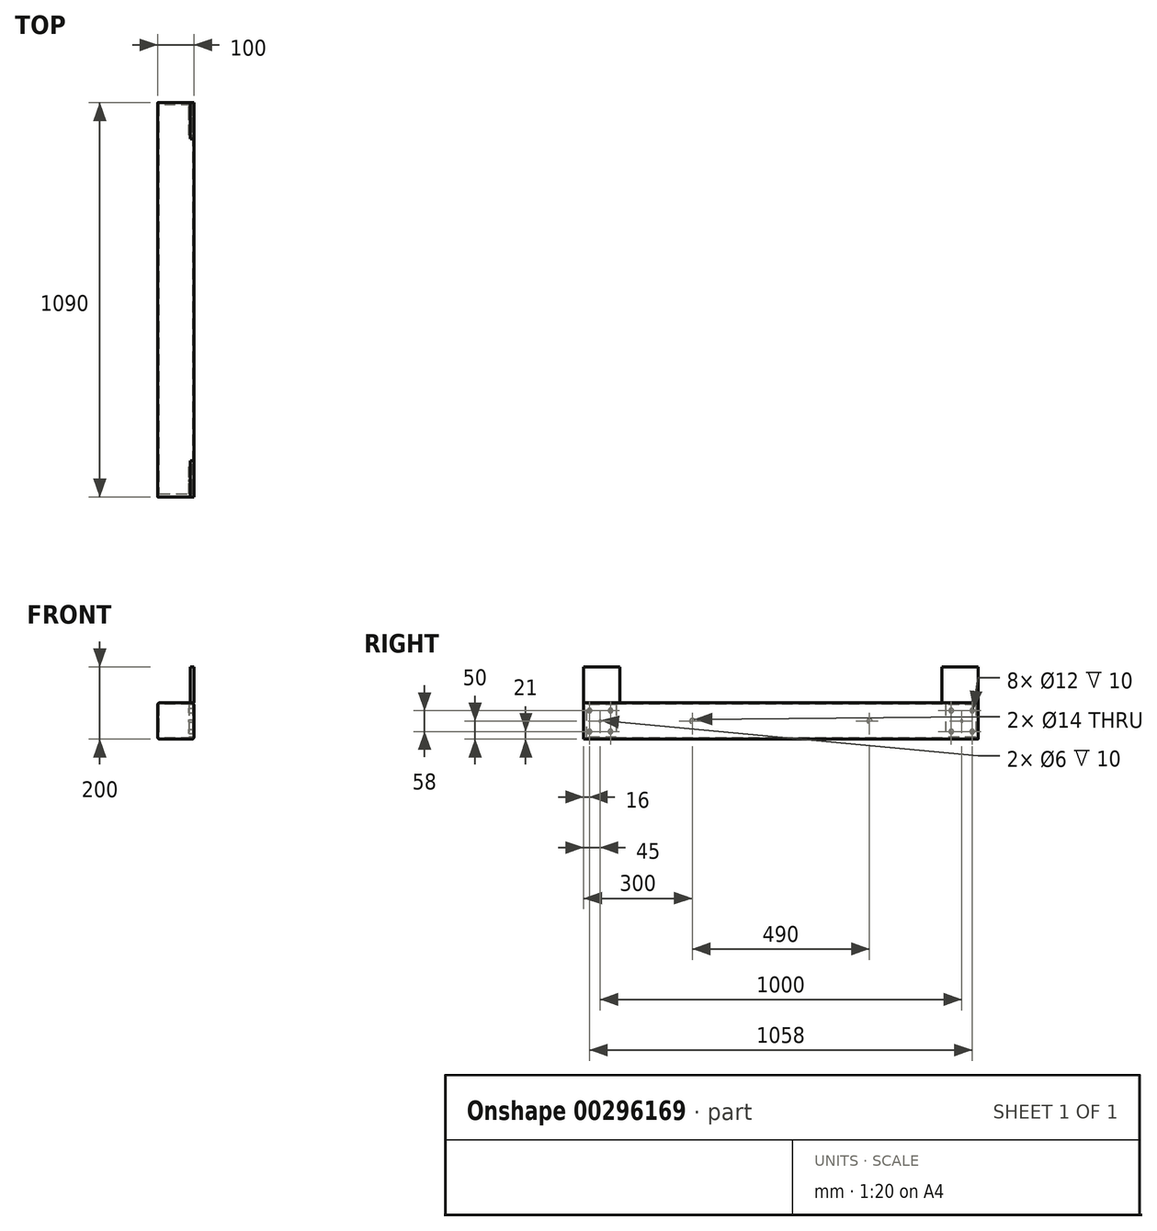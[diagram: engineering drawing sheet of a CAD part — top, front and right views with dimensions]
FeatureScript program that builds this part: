
annotation { "Feature Type Name" : "Feature", "Feature Type Description" : "" }
export const myFeature = defineFeature(function(context is Context, id is Id, definition is map)
    precondition{}
    {
        {
            var Q0;
            Q0=qCreatedBy(makeId("Front.planeOp"),FACE);
            var sketch = newSketch(context, id + "F0", { "sketchPlane" : qUnion([Q0])});
            skLineSegment(sketch, "E0.bottom", {"start": v(45, 50) * mm, "end": v(-45, 50) * mm});
            skLineSegment(sketch, "E0.top", {"start": v(45, -50) * mm, "end": v(-45, -50) * mm});
            skLineSegment(sketch, "E0.left", {"start": v(50, 45) * mm, "end": v(50, -45) * mm});
            skLineSegment(sketch, "E0.right", {"start": v(-50, 45) * mm, "end": v(-50, -45) * mm});
            skPoint(sketch, "E0.middle", {"position": v(0, 0) * mm});
            skPoint(sketch, "E1.visualSharp", {"position": v(-50, 50) * mm});
            skArc(sketch, "E1.filletArc", {"start": v(-45, 50) * mm, "mid": v(-48.54, 48.54) * mm, "end": v(-50, 45) * mm});
            skPoint(sketch, "E2.visualSharp", {"position": v(50, 50) * mm});
            skArc(sketch, "E2.filletArc", {"start": v(50, 45) * mm, "mid": v(48.54, 48.54) * mm, "end": v(45, 50) * mm});
            skPoint(sketch, "E3.visualSharp", {"position": v(50, -50) * mm});
            skArc(sketch, "E3.filletArc", {"start": v(45, -50) * mm, "mid": v(48.54, -48.54) * mm, "end": v(50, -45) * mm});
            skPoint(sketch, "E4.visualSharp", {"position": v(-50, -50) * mm});
            skArc(sketch, "E4.filletArc", {"start": v(-50, -45) * mm, "mid": v(-48.54, -48.54) * mm, "end": v(-45, -50) * mm});
            skArc(sketch, "E5.0", {"start": v(-45, 47) * mm, "mid": v(-46.41, 46.41) * mm, "end": v(-47, 45) * mm});
            skLineSegment(sketch, "E5.1", {"start": v(45, 47) * mm, "end": v(-45, 47) * mm});
            skLineSegment(sketch, "E5.2", {"start": v(-47, 45) * mm, "end": v(-47, -45) * mm});
            skArc(sketch, "E5.3", {"start": v(47, 45) * mm, "mid": v(46.41, 46.41) * mm, "end": v(45, 47) * mm});
            skArc(sketch, "E5.4", {"start": v(-47, -45) * mm, "mid": v(-46.41, -46.41) * mm, "end": v(-45, -47) * mm});
            skLineSegment(sketch, "E5.5", {"start": v(45, -47) * mm, "end": v(-45, -47) * mm});
            skArc(sketch, "E5.6", {"start": v(45, -47) * mm, "mid": v(46.41, -46.41) * mm, "end": v(47, -45) * mm});
            skLineSegment(sketch, "E5.7", {"start": v(47, 45) * mm, "end": v(47, -45) * mm});
            skSolve(sketch);
        }
        {
            var Q0;
            Q0=makeQuery(id+"F0.imprint","IMPRINT",FACE,{"disambiguationData":[TD([[makeQuery(id+"F0.imprint","IMPRINT",EDGE,{"derivedFrom":sQuery(id+"F0.wireOp",EDGE,"E0.bottom")}),1.0]])]});
            extrude(context, id + "F1", {"entities" : qUnion([Q0]), "oppositeDirection" : true, "depth" : (800 + 100 + 100 * 2 - 2 * 5 - 2 * 6) * mm});
        }
        {
            var Q0;
            Q0=makeQuery(id+"F1.opExtrude","CAP_FACE",FACE,{"disambiguationData":[OSD([sQuery(id+"F0.wireOp",EDGE,"E0.bottom"),sQuery(id+"F0.wireOp",EDGE,"E0.top"),sQuery(id+"F0.wireOp",EDGE,"E0.left"),sQuery(id+"F0.wireOp",EDGE,"E0.right"),sQuery(id+"F0.wireOp",EDGE,"E1.filletArc"),sQuery(id+"F0.wireOp",EDGE,"E2.filletArc"),sQuery(id+"F0.wireOp",EDGE,"E3.filletArc"),sQuery(id+"F0.wireOp",EDGE,"E4.filletArc"),sQuery(id+"F0.wireOp",EDGE,"E5.0"),sQuery(id+"F0.wireOp",EDGE,"E5.1"),sQuery(id+"F0.wireOp",EDGE,"E5.2"),sQuery(id+"F0.wireOp",EDGE,"E5.3"),sQuery(id+"F0.wireOp",EDGE,"E5.4"),sQuery(id+"F0.wireOp",EDGE,"E5.5"),sQuery(id+"F0.wireOp",EDGE,"E5.6"),sQuery(id+"F0.wireOp",EDGE,"E5.7")])],"isStart":true});
            cPlane(context, id + "F2", {"entities" : qUnion([Q0]), "cplaneType" : CPlaneType.OFFSET, "offset" : 6 * mm, "width" : 150 * mm, "height" : 150 * mm});
        }
        {
            var Q0;
            Q0=qCreatedBy(id+"F2.planeOp",FACE);
            var sketch = newSketch(context, id + "F3", { "sketchPlane" : qUnion([Q0])});
            skLineSegment(sketch, "E6.bottom", {"start": v(45, 50) * mm, "end": v(-45, 50) * mm});
            skLineSegment(sketch, "E6.top", {"start": v(45, -50) * mm, "end": v(-45, -50) * mm});
            skLineSegment(sketch, "E6.left", {"start": v(50, 45) * mm, "end": v(50, -45) * mm});
            skLineSegment(sketch, "E6.right", {"start": v(-50, 45) * mm, "end": v(-50, -45) * mm});
            skPoint(sketch, "E6.middle", {"position": v(0, 0) * mm});
            skPoint(sketch, "E7.visualSharp", {"position": v(-50, 50) * mm});
            skArc(sketch, "E7.filletArc", {"start": v(-45, 50) * mm, "mid": v(-48.54, 48.54) * mm, "end": v(-50, 45) * mm});
            skPoint(sketch, "E8.visualSharp", {"position": v(50, 50) * mm});
            skArc(sketch, "E8.filletArc", {"start": v(50, 45) * mm, "mid": v(48.54, 48.54) * mm, "end": v(45, 50) * mm});
            skPoint(sketch, "E9.visualSharp", {"position": v(50, -50) * mm});
            skArc(sketch, "E9.filletArc", {"start": v(45, -50) * mm, "mid": v(48.54, -48.54) * mm, "end": v(50, -45) * mm});
            skPoint(sketch, "E10.visualSharp", {"position": v(-50, -50) * mm});
            skArc(sketch, "E10.filletArc", {"start": v(-50, -45) * mm, "mid": v(-48.54, -48.54) * mm, "end": v(-45, -50) * mm});
            skSolve(sketch);
        }
        {
            var Q0;
            Q0=makeQuery(id+"F3.imprint","IMPRINT",FACE,{"disambiguationData":[TD([[makeQuery(id+"F3.imprint","IMPRINT",EDGE,{"derivedFrom":sQuery(id+"F3.wireOp",EDGE,"E6.bottom")}),1.0]])]});
            extrude(context, id + "F4", {"entities" : qUnion([Q0]), "operationType" : NewBodyOperationType.ADD, "oppositeDirection" : true, "depth" : 8 * mm});
        }
        {
            var Q0;
            Q0=makeQuery(id+"F1.opExtrude","CAP_FACE",FACE,{"disambiguationData":[OSD([sQuery(id+"F0.wireOp",EDGE,"E0.bottom"),sQuery(id+"F0.wireOp",EDGE,"E0.top"),sQuery(id+"F0.wireOp",EDGE,"E0.left"),sQuery(id+"F0.wireOp",EDGE,"E0.right"),sQuery(id+"F0.wireOp",EDGE,"E1.filletArc"),sQuery(id+"F0.wireOp",EDGE,"E2.filletArc"),sQuery(id+"F0.wireOp",EDGE,"E3.filletArc"),sQuery(id+"F0.wireOp",EDGE,"E4.filletArc"),sQuery(id+"F0.wireOp",EDGE,"E5.0"),sQuery(id+"F0.wireOp",EDGE,"E5.1"),sQuery(id+"F0.wireOp",EDGE,"E5.2"),sQuery(id+"F0.wireOp",EDGE,"E5.3"),sQuery(id+"F0.wireOp",EDGE,"E5.4"),sQuery(id+"F0.wireOp",EDGE,"E5.5"),sQuery(id+"F0.wireOp",EDGE,"E5.6"),sQuery(id+"F0.wireOp",EDGE,"E5.7")])],"isStart":false});
            cPlane(context, id + "F5", {"entities" : qUnion([Q0]), "cplaneType" : CPlaneType.OFFSET, "offset" : 6 * mm, "width" : 150 * mm, "height" : 150 * mm});
        }
        {
            var Q0;
            Q0=qCreatedBy(id+"F5.planeOp",FACE);
            var sketch = newSketch(context, id + "F6", { "sketchPlane" : qUnion([Q0])});
            skLineSegment(sketch, "E11.bottom", {"start": v(45, 50) * mm, "end": v(-45, 50) * mm});
            skLineSegment(sketch, "E11.top", {"start": v(45, -50) * mm, "end": v(-45, -50) * mm});
            skLineSegment(sketch, "E11.left", {"start": v(50, 45) * mm, "end": v(50, -45) * mm});
            skLineSegment(sketch, "E11.right", {"start": v(-50, 45) * mm, "end": v(-50, -45) * mm});
            skPoint(sketch, "E11.middle", {"position": v(0, 0) * mm});
            skPoint(sketch, "E12.visualSharp", {"position": v(-50, 50) * mm});
            skArc(sketch, "E12.filletArc", {"start": v(-45, 50) * mm, "mid": v(-48.54, 48.54) * mm, "end": v(-50, 45) * mm});
            skPoint(sketch, "E13.visualSharp", {"position": v(50, 50) * mm});
            skArc(sketch, "E13.filletArc", {"start": v(50, 45) * mm, "mid": v(48.54, 48.54) * mm, "end": v(45, 50) * mm});
            skPoint(sketch, "E14.visualSharp", {"position": v(50, -50) * mm});
            skArc(sketch, "E14.filletArc", {"start": v(45, -50) * mm, "mid": v(48.54, -48.54) * mm, "end": v(50, -45) * mm});
            skPoint(sketch, "E15.visualSharp", {"position": v(-50, -50) * mm});
            skArc(sketch, "E15.filletArc", {"start": v(-50, -45) * mm, "mid": v(-48.54, -48.54) * mm, "end": v(-45, -50) * mm});
            skSolve(sketch);
        }
        {
            var Q0;
            Q0=makeQuery(id+"F6.imprint","IMPRINT",FACE,{"disambiguationData":[TD([[makeQuery(id+"F6.imprint","IMPRINT",EDGE,{"derivedFrom":sQuery(id+"F6.wireOp",EDGE,"E11.bottom")}),1.0]])]});
            extrude(context, id + "F7", {"entities" : qUnion([Q0]), "oppositeDirection" : true, "depth" : 6 * mm});
        }
        {
            var Q0;
            Q0=makeQuery(id+"F7.opExtrude","SWEPT_BODY",BODY,{"disambiguationData":[OSD([sQuery(id+"F6.wireOp",EDGE,"E11.bottom"),sQuery(id+"F6.wireOp",EDGE,"E11.top"),sQuery(id+"F6.wireOp",EDGE,"E11.left"),sQuery(id+"F6.wireOp",EDGE,"E11.right"),sQuery(id+"F6.wireOp",EDGE,"E12.filletArc"),sQuery(id+"F6.wireOp",EDGE,"E13.filletArc"),sQuery(id+"F6.wireOp",EDGE,"E14.filletArc"),sQuery(id+"F6.wireOp",EDGE,"E15.filletArc")])]});
            var Q1;
            Q1=makeQuery(id+"F1.opExtrude","SWEPT_BODY",BODY,{"disambiguationData":[OSD([sQuery(id+"F0.wireOp",EDGE,"E0.bottom"),sQuery(id+"F0.wireOp",EDGE,"E0.top"),sQuery(id+"F0.wireOp",EDGE,"E0.left"),sQuery(id+"F0.wireOp",EDGE,"E0.right"),sQuery(id+"F0.wireOp",EDGE,"E1.filletArc"),sQuery(id+"F0.wireOp",EDGE,"E2.filletArc"),sQuery(id+"F0.wireOp",EDGE,"E3.filletArc"),sQuery(id+"F0.wireOp",EDGE,"E4.filletArc"),sQuery(id+"F0.wireOp",EDGE,"E5.0"),sQuery(id+"F0.wireOp",EDGE,"E5.1"),sQuery(id+"F0.wireOp",EDGE,"E5.2"),sQuery(id+"F0.wireOp",EDGE,"E5.3"),sQuery(id+"F0.wireOp",EDGE,"E5.4"),sQuery(id+"F0.wireOp",EDGE,"E5.5"),sQuery(id+"F0.wireOp",EDGE,"E5.6"),sQuery(id+"F0.wireOp",EDGE,"E5.7")])]});
            booleanBodies(context, id + "F8", {"operationType" : BooleanOperationType.UNION, "tools" : qUnion([Q0, Q1])});
        }
        {
            var Q0;
            Q0=makeQuery(id+"F8.opBoolean","MERGE",FACE,{"derivedFrom":[makeQuery(id+"F4.boolean.opBoolean","MERGE",FACE,{"derivedFrom":[makeQuery(id+"F1.opExtrude","SWEPT_FACE",FACE,{"disambiguationData":[OSD([sQuery(id+"F0.wireOp",EDGE,"E0.right")])]}),makeQuery(id+"F4.opExtrude","SWEPT_FACE",FACE,{"disambiguationData":[OSD([sQuery(id+"F3.wireOp",EDGE,"E6.right")])]})]}),makeQuery(id+"F7.opExtrude","SWEPT_FACE",FACE,{"disambiguationData":[OSD([sQuery(id+"F6.wireOp",EDGE,"E11.left")])]})]});
            var sketch = newSketch(context, id + "F9", { "sketchPlane" : qUnion([Q0])});
            skCircle(sketch, "E16", {"center": v(-294, 0) * mm, "radius": 7 * mm});
            skCircle(sketch, "E17", {"center": v(-784, 0) * mm, "radius": 7 * mm});
            skLineSegment(sketch, "E18", {"start": v(-1084, 0) * mm, "end": v(0, 0) * mm, "construction": true});
            skSolve(sketch);
        }
        {
            var Q0;
            Q0=makeQuery(id+"F9.imprint","IMPRINT",FACE,{"disambiguationData":[TD([[makeQuery(id+"F9.imprint","IMPRINT",EDGE,{"derivedFrom":sQuery(id+"F9.wireOp",EDGE,"E17")}),1.0]])]});
            var Q1;
            Q1=makeQuery(id+"F9.imprint","IMPRINT",FACE,{"disambiguationData":[TD([[makeQuery(id+"F9.imprint","IMPRINT",EDGE,{"derivedFrom":sQuery(id+"F9.wireOp",EDGE,"E16")}),1.0]])]});
            extrude(context, id + "F10", {"entities" : qUnion([Q0, Q1]), "operationType" : NewBodyOperationType.REMOVE, "endBound" : BoundingType.UP_TO_NEXT, "oppositeDirection" : true, "depth" : 25 * mm});
        }
        {
            var Q0;
            Q0=makeQuery(id+"F8.opBoolean","MERGE",FACE,{"derivedFrom":[makeQuery(id+"F4.boolean.opBoolean","MERGE",FACE,{"derivedFrom":[makeQuery(id+"F1.opExtrude","SWEPT_FACE",FACE,{"disambiguationData":[OSD([sQuery(id+"F0.wireOp",EDGE,"E0.left")])]}),makeQuery(id+"F4.opExtrude","SWEPT_FACE",FACE,{"disambiguationData":[OSD([sQuery(id+"F3.wireOp",EDGE,"E6.left")])]})]}),makeQuery(id+"F7.opExtrude","SWEPT_FACE",FACE,{"disambiguationData":[OSD([sQuery(id+"F6.wireOp",EDGE,"E11.right")])]})]});
            var sketch = newSketch(context, id + "F11", { "sketchPlane" : qUnion([Q0])});
            skLineSegment(sketch, "E19.bottom", {"start": v(-6, -45) * mm, "end": v(84, -45) * mm});
            skLineSegment(sketch, "E19.top", {"start": v(-6, 45) * mm, "end": v(84, 45) * mm});
            skLineSegment(sketch, "E19.left", {"start": v(-6, -45) * mm, "end": v(-6, 45) * mm});
            skLineSegment(sketch, "E19.right", {"start": v(84, -45) * mm, "end": v(84, 45) * mm});
            skPoint(sketch, "E19.middle", {"position": v(39, 0) * mm});
            skLineSegment(sketch, "E20", {"start": v(84, 45) * mm, "end": v(-6, -45) * mm, "construction": true});
            skLineSegment(sketch, "E21", {"start": v(-6, 45) * mm, "end": v(84, -45) * mm, "construction": true});
            skLineSegment(sketch, "E22", {"start": v(84, -29) * mm, "end": v(-6, -29) * mm, "construction": true});
            skCircle(sketch, "E23", {"center": v(10, -29) * mm, "radius": 6 * mm});
            skCircle(sketch, "E24", {"center": v(68, -29) * mm, "radius": 6 * mm});
            skLineSegment(sketch, "E25", {"start": v(68, -29) * mm, "end": v(68, 29) * mm, "construction": true});
            skLineSegment(sketch, "E26", {"start": v(68, 29) * mm, "end": v(10, 29) * mm, "construction": true});
            skCircle(sketch, "E27", {"center": v(10, 29) * mm, "radius": 6 * mm});
            skCircle(sketch, "E28", {"center": v(68, 29) * mm, "radius": 6 * mm});
            skCircle(sketch, "E29", {"center": v(39, 0) * mm, "radius": 3 * mm});
            skLineSegment(sketch, "E30.bottom", {"start": v(994, -45) * mm, "end": v(1084, -45) * mm});
            skLineSegment(sketch, "E30.top", {"start": v(994, 45) * mm, "end": v(1084, 45) * mm});
            skLineSegment(sketch, "E30.left", {"start": v(994, -45) * mm, "end": v(994, 45) * mm});
            skLineSegment(sketch, "E30.right", {"start": v(1084, -45) * mm, "end": v(1084, 45) * mm});
            skPoint(sketch, "E30.middle", {"position": v(1039, 0) * mm});
            skLineSegment(sketch, "E31", {"start": v(1084, 45) * mm, "end": v(994, -45) * mm, "construction": true});
            skLineSegment(sketch, "E32", {"start": v(994, 45) * mm, "end": v(1084, -45) * mm, "construction": true});
            skLineSegment(sketch, "E33", {"start": v(1084, -29) * mm, "end": v(994, -29) * mm, "construction": true});
            skCircle(sketch, "E34", {"center": v(1010, -29) * mm, "radius": 6 * mm});
            skCircle(sketch, "E35", {"center": v(1068, -29) * mm, "radius": 6 * mm});
            skLineSegment(sketch, "E36", {"start": v(1068, -29) * mm, "end": v(1068, 29) * mm, "construction": true});
            skLineSegment(sketch, "E37", {"start": v(1068, 29) * mm, "end": v(1010, 29) * mm, "construction": true});
            skCircle(sketch, "E38", {"center": v(1010, 29) * mm, "radius": 6 * mm});
            skCircle(sketch, "E39", {"center": v(1068, 29) * mm, "radius": 6 * mm});
            skCircle(sketch, "E40", {"center": v(1039, 0) * mm, "radius": 3 * mm});
            skSolve(sketch);
        }
        {
            var Q0;
            Q0=makeQuery(id+"F11.imprint","IMPRINT",FACE,{"disambiguationData":[TD([[makeQuery(id+"F11.imprint","IMPRINT",EDGE,{"derivedFrom":sQuery(id+"F11.wireOp",EDGE,"E30.bottom")}),1.0]])]});
            var Q1;
            Q1=makeQuery(id+"F11.imprint","IMPRINT",FACE,{"disambiguationData":[TD([[makeQuery(id+"F11.imprint","IMPRINT",EDGE,{"derivedFrom":sQuery(id+"F11.wireOp",EDGE,"E19.bottom")}),1.0]])]});
            extrude(context, id + "F12", {"entities" : qUnion([Q0, Q1]), "operationType" : NewBodyOperationType.ADD, "oppositeDirection" : true, "depth" : 13 * mm});
        }
        {
            var Q0;
            Q0=makeQuery(id+"F8.opBoolean","MERGE",FACE,{"derivedFrom":[makeQuery(id+"F4.boolean.opBoolean","MERGE",FACE,{"derivedFrom":[makeQuery(id+"F1.opExtrude","SWEPT_FACE",FACE,{"disambiguationData":[OSD([sQuery(id+"F0.wireOp",EDGE,"E0.bottom")])]}),makeQuery(id+"F4.opExtrude","SWEPT_FACE",FACE,{"disambiguationData":[OSD([sQuery(id+"F3.wireOp",EDGE,"E6.bottom")])]})]}),makeQuery(id+"F7.opExtrude","SWEPT_FACE",FACE,{"disambiguationData":[OSD([sQuery(id+"F6.wireOp",EDGE,"E11.bottom")])]})]});
            var sketch = newSketch(context, id + "F13", { "sketchPlane" : qUnion([Q0])});
            skLineSegment(sketch, "E41.bottom", {"start": v(50, 1084) * mm, "end": v(40, 1084) * mm});
            skLineSegment(sketch, "E41.top", {"start": v(50, 984) * mm, "end": v(40, 984) * mm});
            skLineSegment(sketch, "E41.left", {"start": v(50, 1084) * mm, "end": v(50, 984) * mm});
            skLineSegment(sketch, "E41.right", {"start": v(40, 1084) * mm, "end": v(40, 984) * mm});
            skLineSegment(sketch, "E42.bottom", {"start": v(50, 94) * mm, "end": v(40, 94) * mm});
            skLineSegment(sketch, "E42.top", {"start": v(50, -6) * mm, "end": v(40, -6) * mm});
            skLineSegment(sketch, "E42.left", {"start": v(50, 94) * mm, "end": v(50, -6) * mm});
            skLineSegment(sketch, "E42.right", {"start": v(40, 94) * mm, "end": v(40, -6) * mm});
            skLineSegment(sketch, "E43.bottom", {"start": v(-50, 94) * mm, "end": v(-60, 94) * mm});
            skLineSegment(sketch, "E43.top", {"start": v(-50, -6) * mm, "end": v(-60, -6) * mm});
            skLineSegment(sketch, "E43.left", {"start": v(-50, 94) * mm, "end": v(-50, -6) * mm});
            skLineSegment(sketch, "E43.right", {"start": v(-60, 94) * mm, "end": v(-60, -6) * mm});
            skLineSegment(sketch, "E44.bottom", {"start": v(-40, 1084) * mm, "end": v(-50, 1084) * mm});
            skLineSegment(sketch, "E44.top", {"start": v(-40, 984) * mm, "end": v(-50, 984) * mm});
            skLineSegment(sketch, "E44.left", {"start": v(-40, 1084) * mm, "end": v(-40, 984) * mm});
            skLineSegment(sketch, "E44.right", {"start": v(-50, 1084) * mm, "end": v(-50, 984) * mm});
            skSolve(sketch);
        }
        {
            var Q0;
            {var subQ3=sQuery(id+"F13.wireOp",EDGE,"E41.left");Q0=makeQuery(id+"F13.imprint","IMPRINT",FACE,{"disambiguationData":[TD([[makeQuery(id+"F13.imprint","IMPRINT",EDGE,{"derivedFrom":subQ3}),-1.0]])]});}
            var Q1;
            {var subQ4=sQuery(id+"F13.wireOp",EDGE,"E41.right");Q1=makeQuery(id+"F13.imprint","IMPRINT",FACE,{"disambiguationData":[TD([[makeQuery(id+"F13.imprint","IMPRINT",EDGE,{"derivedFrom":subQ4}),1.0]])]});}
            var Q2;
            Q2=makeQuery(id+"F13.imprint","IMPRINT",FACE,{"disambiguationData":[TD([[makeQuery(id+"F13.imprint","IMPRINT",EDGE,{"derivedFrom":sQuery(id+"F13.wireOp",EDGE,"E42.bottom")}),1.0]])]});
            extrude(context, id + "F14", {"entities" : qUnion([Q0, Q1, Q2]), "depth" : 100 * mm});
        }
    });
